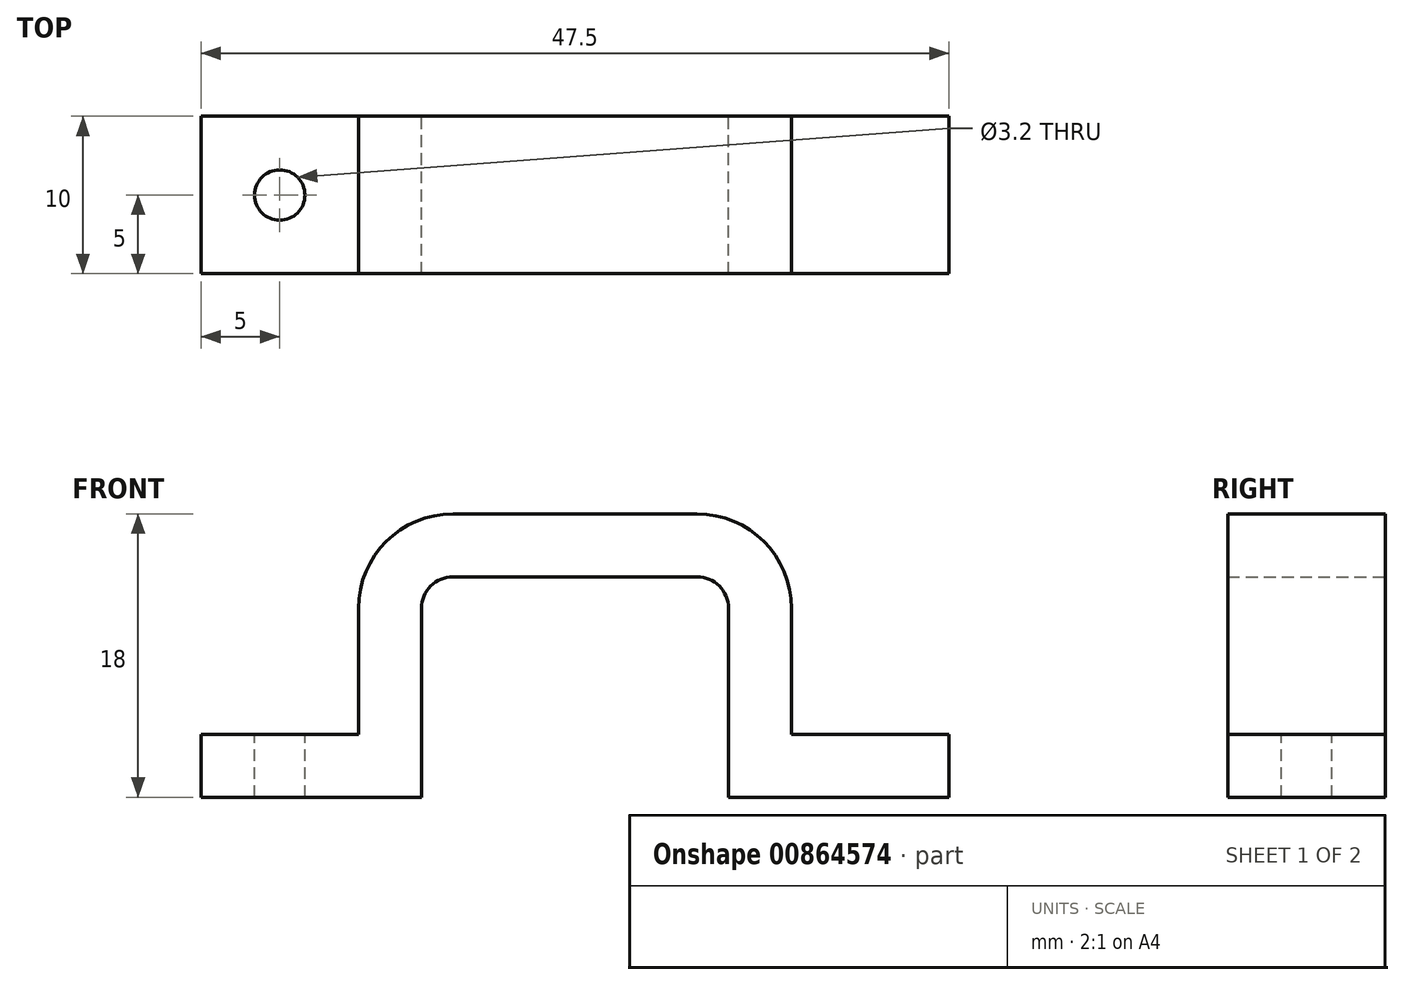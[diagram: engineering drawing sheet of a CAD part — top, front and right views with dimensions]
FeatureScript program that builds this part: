
annotation { "Feature Type Name" : "Feature", "Feature Type Description" : "" }
export const myFeature = defineFeature(function(context is Context, id is Id, definition is map)
    precondition{}
    {
        {
            assignVariable(context, id + "F0", {"name" : "l_bracket", "anyValue" : 10});
        }
        {
            var Q0;
            Q0=qCreatedBy(makeId("Front.planeOp"),FACE);
            var sketch = newSketch(context, id + "F1", { "sketchPlane" : qUnion([Q0])});
            skLineSegment(sketch, "E0.bottom", {"start": v(-9.75, 0) * mm, "end": v(9.75, 0) * mm});
            skLineSegment(sketch, "E0.top", {"start": v(-7.75, 14) * mm, "end": v(7.75, 14) * mm});
            skLineSegment(sketch, "E0.left", {"start": v(-9.75, 0) * mm, "end": v(-9.75, 12) * mm});
            skLineSegment(sketch, "E0.right", {"start": v(9.75, 0) * mm, "end": v(9.75, 12) * mm});
            skPoint(sketch, "E1.visualSharp", {"position": v(-9.75, 14) * mm});
            skArc(sketch, "E1.filletArc", {"start": v(-7.75, 14) * mm, "mid": v(-9.16, 13.41) * mm, "end": v(-9.75, 12) * mm});
            skPoint(sketch, "E2.visualSharp", {"position": v(9.75, 14) * mm});
            skArc(sketch, "E2.filletArc", {"start": v(9.75, 12) * mm, "mid": v(9.16, 13.41) * mm, "end": v(7.75, 14) * mm});
            skLineSegment(sketch, "E3.0", {"start": v(13.75, 0) * mm, "end": v(13.75, 12) * mm});
            skLineSegment(sketch, "E3.1", {"start": v(-13.75, 0) * mm, "end": v(-13.75, 12) * mm});
            skArc(sketch, "E3.2", {"start": v(-7.75, 18) * mm, "mid": v(-12, 16.24) * mm, "end": v(-13.75, 12) * mm});
            skLineSegment(sketch, "E3.3", {"start": v(-7.75, 18) * mm, "end": v(7.75, 18) * mm});
            skArc(sketch, "E3.4", {"start": v(13.75, 12) * mm, "mid": v(12, 16.24) * mm, "end": v(7.75, 18) * mm});
            skLineSegment(sketch, "E4", {"start": v(-9.75, 0) * mm, "end": v(-13.75, 0) * mm});
            skLineSegment(sketch, "E5", {"start": v(9.75, 0) * mm, "end": v(13.75, 0) * mm});
            skLineSegment(sketch, "E6.bottom", {"start": v(13.75, 0) * mm, "end": v(23.75, 0) * mm});
            skLineSegment(sketch, "E6.top", {"start": v(13.75, 4) * mm, "end": v(23.75, 4) * mm});
            skLineSegment(sketch, "E6.left", {"start": v(13.75, 0) * mm, "end": v(13.75, 4) * mm});
            skLineSegment(sketch, "E6.right", {"start": v(23.75, 0) * mm, "end": v(23.75, 4) * mm});
            skLineSegment(sketch, "E7.MirrorCS", {"start": v(-13.75, 4) * mm, "end": v(-23.75, 4) * mm});
            skLineSegment(sketch, "E8.MirrorCS", {"start": v(-23.75, 0) * mm, "end": v(-23.75, 4) * mm});
            skLineSegment(sketch, "E9.MirrorCS", {"start": v(-13.75, 0) * mm, "end": v(-23.75, 0) * mm});
            skSolve(sketch);
        }
        {
            var Q0;
            Q0=makeQuery(id+"F1.imprint","IMPRINT",FACE,{"disambiguationData":[TD([[makeQuery(id+"F1.imprint","IMPRINT",EDGE,{"derivedFrom":sQuery(id+"F1.wireOp",EDGE,"E0.top")}),1.0]])]});
            var Q1;
            {var subQ2=sQuery(id+"F1.wireOp",EDGE,"E6.bottom");Q1=makeQuery(id+"F1.imprint","IMPRINT",FACE,{"disambiguationData":[TD([[makeQuery(id+"F1.imprint","IMPRINT",EDGE,{"derivedFrom":subQ2}),1.0]])]});}
            var Q2;
            {var subQ0=sQuery(id+"F1.wireOp",EDGE,"E7.MirrorCS");Q2=makeQuery(id+"F1.imprint","IMPRINT",FACE,{"disambiguationData":[TD([[makeQuery(id+"F1.imprint","IMPRINT",EDGE,{"derivedFrom":subQ0}),1.0]])]});}
            extrude(context, id + "F2", {"entities" : qUnion([Q0, Q1, Q2]), "depth" : (getVariable(context, 'l_bracket')) * mm, "offsetDistance" : 25 * mm, "symmetric" : true});
        }
        {
            var Q0;
            Q0=makeQuery(id+"F2.opExtrude","SWEPT_FACE",FACE,{"disambiguationData":[OSD([sQuery(id+"F1.wireOp",EDGE,"E7.MirrorCS")])]});
            var sketch = newSketch(context, id + "F3", { "sketchPlane" : qUnion([Q0])});
            skLineSegment(sketch, "E10", {"start": v(-23.75, 0) * mm, "end": v(-13.75, 0) * mm, "construction": true});
            skCircle(sketch, "E11", {"center": v(-18.75, 0) * mm, "radius": 1.6 * mm});
            skCircle(sketch, "E12.MirrorC", {"center": v(18.75, 0) * mm, "radius": 1.6 * mm});
            skSolve(sketch);
        }
        {
            var Q0;
            Q0=makeQuery(id+"F3.imprint","IMPRINT",FACE,{"disambiguationData":[TD([[makeQuery(id+"F3.imprint","IMPRINT",EDGE,{"derivedFrom":sQuery(id+"F3.wireOp",EDGE,"E11")}),1.0]])]});
            var Q1;
            Q1=makeQuery(id+"F3.imprint","IMPRINT",FACE,{"disambiguationData":[TD([[makeQuery(id+"F3.imprint","IMPRINT",EDGE,{"derivedFrom":sQuery(id+"F3.wireOp",EDGE,"E12.MirrorC")}),-1.0]])]});
            var Q2;
            Q2=sQuery(id+"F3.wireOp",EDGE,"E11");
            var Q3;
            Q3=sQuery(id+"F3.wireOp",EDGE,"E12.MirrorC");
            extrude(context, id + "F4", {"entities" : qUnion([Q0, Q1]), "operationType" : NewBodyOperationType.REMOVE, "surfaceEntities" : qUnion([Q2, Q3]), "endBound" : BoundingType.THROUGH_ALL, "oppositeDirection" : true, "depth" : 25 * mm, "offsetDistance" : 25 * mm});
        }
    });
